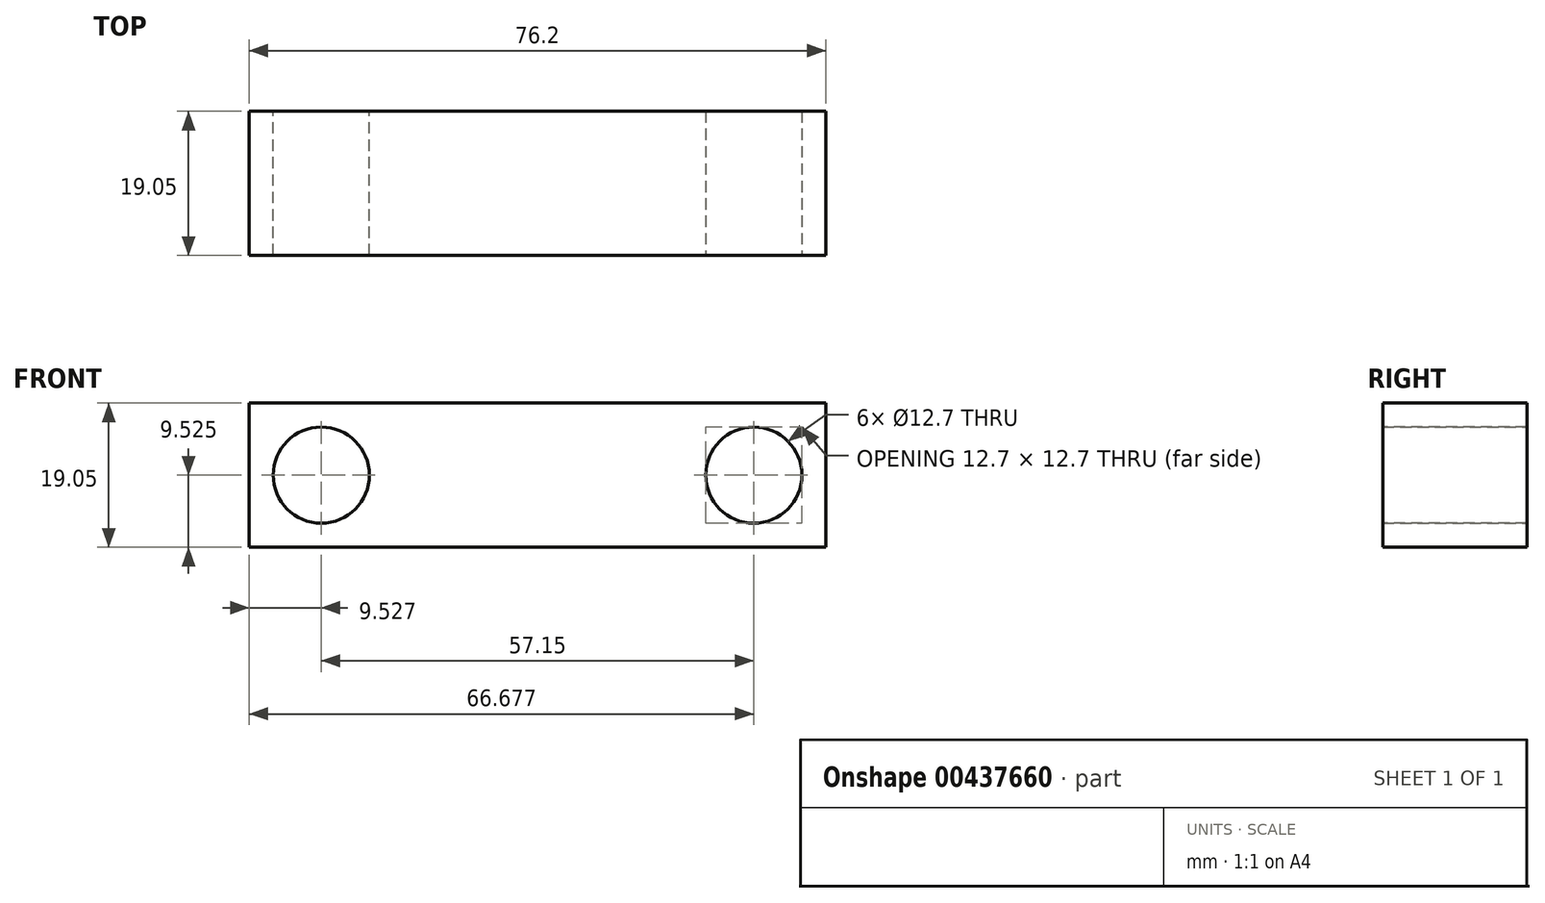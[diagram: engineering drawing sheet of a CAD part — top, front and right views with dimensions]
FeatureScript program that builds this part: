
annotation { "Feature Type Name" : "Feature", "Feature Type Description" : "" }
export const myFeature = defineFeature(function(context is Context, id is Id, definition is map)
    precondition{}
    {
        {
            var Q0;
            Q0=qCreatedBy(makeId("Top.planeOp"),FACE);
            var sketch = newSketch(context, id + "F0", { "sketchPlane" : qUnion([Q0])});
            skLineSegment(sketch, "E0.bottom", {"start": v(-28.48, 5.03) * mm, "end": v(47.72, 5.03) * mm});
            skLineSegment(sketch, "E0.top", {"start": v(-28.48, -14.02) * mm, "end": v(47.72, -14.02) * mm});
            skLineSegment(sketch, "E0.left", {"start": v(-28.48, 5.03) * mm, "end": v(-28.48, -14.02) * mm});
            skLineSegment(sketch, "E0.right", {"start": v(47.72, 5.03) * mm, "end": v(47.72, -14.02) * mm});
            skSolve(sketch);
        }
        {
            var Q0;
            Q0=makeQuery(id+"F0.imprint","IMPRINT",FACE,{"disambiguationData":[TD([[makeQuery(id+"F0.imprint","IMPRINT",EDGE,{"derivedFrom":sQuery(id+"F0.wireOp",EDGE,"E0.bottom")}),-1.0]])]});
            extrude(context, id + "F1", {"entities" : qUnion([Q0]), "depth" : 19.05 * mm});
        }
        {
            var Q0;
            Q0=makeQuery(id+"F1.opExtrude","SWEPT_FACE",FACE,{"disambiguationData":[OSD([sQuery(id+"F0.wireOp",EDGE,"E0.bottom")])]});
            var sketch = newSketch(context, id + "F2", { "sketchPlane" : qUnion([Q0])});
            skPoint(sketch, "E1", {"position": v(18.95, 9.53) * mm});
            skSolve(sketch);
        }
        {
            var Q0;
            Q0=sQuery(id+"F2.wireOp",VERTEX,"E1");
            var Q1;
            Q1=makeQuery(id+"F1.opExtrude","SWEPT_BODY",BODY,{"disambiguationData":[OSD([sQuery(id+"F0.wireOp",EDGE,"E0.bottom"),sQuery(id+"F0.wireOp",EDGE,"E0.top"),sQuery(id+"F0.wireOp",EDGE,"E0.left"),sQuery(id+"F0.wireOp",EDGE,"E0.right")])]});
            hole(context, id + "F3", {"style" : HoleStyle.SIMPLE, "endStyle" : HoleEndStyle.THROUGH, "holeDiameter" : 12.7 * mm, "isTappedThrough" : true, "tappedDepth" : 12.7 * mm, "tapClearance" : 3, "locations" : qUnion([Q0]), "scope" : qUnion([Q1])});
        }
        {
            var Q0;
            Q0=makeQuery(id+"F1.opExtrude","SWEPT_FACE",FACE,{"disambiguationData":[OSD([sQuery(id+"F0.wireOp",EDGE,"E0.top")])]});
            var sketch = newSketch(context, id + "F4", { "sketchPlane" : qUnion([Q0])});
            skPoint(sketch, "E2", {"position": v(38.2, 9.53) * mm});
            skSolve(sketch);
        }
        {
            var Q0;
            Q0=sQuery(id+"F4.wireOp",VERTEX,"E2");
            var Q1;
            Q1=makeQuery(id+"F1.opExtrude","SWEPT_BODY",BODY,{"disambiguationData":[OSD([sQuery(id+"F0.wireOp",EDGE,"E0.bottom"),sQuery(id+"F0.wireOp",EDGE,"E0.top"),sQuery(id+"F0.wireOp",EDGE,"E0.left"),sQuery(id+"F0.wireOp",EDGE,"E0.right")])]});
            hole(context, id + "F5", {"style" : HoleStyle.SIMPLE, "endStyle" : HoleEndStyle.THROUGH, "holeDiameter" : 12.7 * mm, "isTappedThrough" : true, "tappedDepth" : 12.7 * mm, "tapClearance" : 3, "locations" : qUnion([Q0]), "scope" : qUnion([Q1])});
        }
    });
